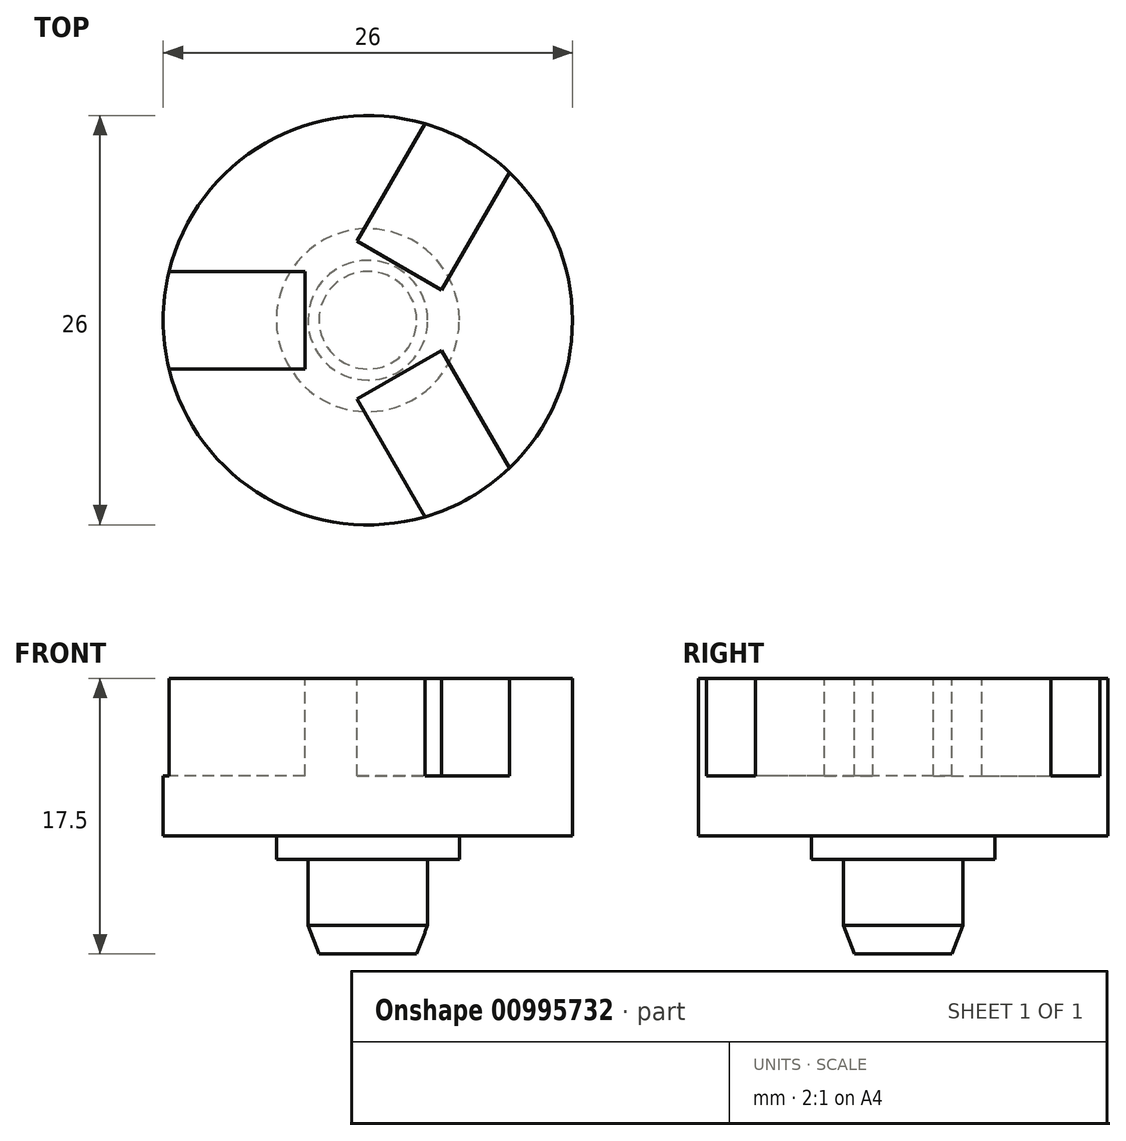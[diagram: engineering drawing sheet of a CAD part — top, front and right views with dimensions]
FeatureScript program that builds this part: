
annotation { "Feature Type Name" : "Feature", "Feature Type Description" : "" }
export const myFeature = defineFeature(function(context is Context, id is Id, definition is map)
    precondition{}
    {
        {
            var Q0;
            Q0=qCreatedBy(makeId("Front.planeOp"),FACE);
            var sketch = newSketch(context, id + "F0", { "sketchPlane" : qUnion([Q0])});
            skLineSegment(sketch, "E0", {"start": v(0, 0) * mm, "end": v(3.1, 0) * mm});
            skLineSegment(sketch, "E1", {"start": v(3.1, 0) * mm, "end": v(3.8, 1.83) * mm});
            skLineSegment(sketch, "E2", {"start": v(3.8, 1.83) * mm, "end": v(3.8, 6) * mm});
            skLineSegment(sketch, "E3", {"start": v(3.8, 6) * mm, "end": v(5.81, 6) * mm});
            skLineSegment(sketch, "E4", {"start": v(5.81, 6) * mm, "end": v(5.81, 7.5) * mm});
            skLineSegment(sketch, "E5", {"start": v(5.81, 7.5) * mm, "end": v(13, 7.5) * mm});
            skLineSegment(sketch, "E6", {"start": v(13, 7.5) * mm, "end": v(13, 17.5) * mm});
            skLineSegment(sketch, "E7", {"start": v(13, 17.5) * mm, "end": v(0, 17.5) * mm});
            skLineSegment(sketch, "E8", {"start": v(0, 17.5) * mm, "end": v(0, 0) * mm});
            skSolve(sketch);
        }
        {
            var Q0;
            Q0=makeQuery(id+"F0.imprint","IMPRINT",FACE,{"disambiguationData":[TD([[makeQuery(id+"F0.imprint","IMPRINT",EDGE,{"derivedFrom":sQuery(id+"F0.wireOp",EDGE,"E0")}),1.0]])]});
            var Q1;
            Q1=sQuery(id+"F0.wireOp",EDGE,"E8");
            revolve(context, id + "F1", {"surfaceOperationType" : NewSurfaceOperationType.NEW, "entities" : qUnion([Q0]), "axis" : qUnion([Q1]), "revolveType" : RevolveType.FULL});
        }
        {
            var Q0;
            Q0=makeQuery(id+"F1.opRevolve","SWEPT_FACE",FACE,{"disambiguationData":[OSD([sQuery(id+"F0.wireOp",EDGE,"E7")])]});
            var sketch = newSketch(context, id + "F2", { "sketchPlane" : qUnion([Q0])});
            skLineSegment(sketch, "E9.bottom", {"start": v(-4, 3.1) * mm, "end": v(-34.21, 3.1) * mm});
            skLineSegment(sketch, "E9.top", {"start": v(-4, -3.1) * mm, "end": v(-34.21, -3.1) * mm});
            skLineSegment(sketch, "E9.left", {"start": v(-4, 3.1) * mm, "end": v(-4, -3.1) * mm});
            skLineSegment(sketch, "E9.right", {"start": v(-34.21, 3.1) * mm, "end": v(-34.21, -3.1) * mm});
            skPoint(sketch, "E9.middle", {"position": v(-19.1, 0) * mm});
            skSolve(sketch);
        }
        {
            var Q0;
            {var subQ0=sQuery(id+"F2.wireOp",EDGE,"E9.left");Q0=makeQuery(id+"F2.imprint","IMPRINT",FACE,{"disambiguationData":[TD([[makeQuery(id+"F2.imprint","IMPRINT",EDGE,{"derivedFrom":subQ0}),-1.0]])]});}
            extrude(context, id + "F3", {"entities" : qUnion([Q0]), "oppositeDirection" : true, "depth" : 6.2 * mm, "offsetDistance" : 25 * mm});
        }
        {
            var Q0;
            Q0=makeQuery(id+"F3.opExtrude","SWEPT_BODY",BODY,{"disambiguationData":[OSD([sQuery(id+"F0.wireOp",EDGE,"E6"),sQuery(id+"F0.wireOp",EDGE,"E7"),sQuery(id+"F2.wireOp",EDGE,"E9.bottom"),sQuery(id+"F2.wireOp",EDGE,"E9.top"),sQuery(id+"F2.wireOp",EDGE,"E9.left")])]});
            var Q1;
            Q1=makeQuery(id+"F1.opRevolve","SWEPT_EDGE",EDGE,{"disambiguationData":[OSD([sQuery(id+"F0.wireOp",EDGE,"E6"),sQuery(id+"F0.wireOp",EDGE,"E7")])]});
            circularPattern(context, id + "F4", {"entities" : qUnion([Q0]), "axis" : qUnion([Q1]), "angle" : 360 * degree, "instanceCount" : 3, "equalSpace" : true});
        }
        {
            var Q0;
            Q0=makeQuery(id+"F3.opExtrude","SWEPT_BODY",BODY,{"disambiguationData":[OSD([sQuery(id+"F0.wireOp",EDGE,"E6"),sQuery(id+"F0.wireOp",EDGE,"E7"),sQuery(id+"F2.wireOp",EDGE,"E9.bottom"),sQuery(id+"F2.wireOp",EDGE,"E9.top"),sQuery(id+"F2.wireOp",EDGE,"E9.left")])]});
            var Q1;
            Q1=makeQuery(id+"F4.opPattern","COPY",BODY,{"derivedFrom":makeQuery(id+"F3.opExtrude","SWEPT_BODY",BODY,{"disambiguationData":[OSD([sQuery(id+"F0.wireOp",EDGE,"E6"),sQuery(id+"F0.wireOp",EDGE,"E7"),sQuery(id+"F2.wireOp",EDGE,"E9.bottom"),sQuery(id+"F2.wireOp",EDGE,"E9.top"),sQuery(id+"F2.wireOp",EDGE,"E9.left")])]}),"instanceName":"1"});
            var Q2;
            Q2=makeQuery(id+"F4.opPattern","COPY",BODY,{"derivedFrom":makeQuery(id+"F3.opExtrude","SWEPT_BODY",BODY,{"disambiguationData":[OSD([sQuery(id+"F0.wireOp",EDGE,"E6"),sQuery(id+"F0.wireOp",EDGE,"E7"),sQuery(id+"F2.wireOp",EDGE,"E9.bottom"),sQuery(id+"F2.wireOp",EDGE,"E9.top"),sQuery(id+"F2.wireOp",EDGE,"E9.left")])]}),"instanceName":"2"});
            var Q3;
            Q3=makeQuery(id+"F1.opRevolve","SWEPT_BODY",BODY,{"disambiguationData":[OSD([sQuery(id+"F0.wireOp",EDGE,"E0"),sQuery(id+"F0.wireOp",EDGE,"E1"),sQuery(id+"F0.wireOp",EDGE,"E2"),sQuery(id+"F0.wireOp",EDGE,"E3"),sQuery(id+"F0.wireOp",EDGE,"E4"),sQuery(id+"F0.wireOp",EDGE,"E5"),sQuery(id+"F0.wireOp",EDGE,"E6"),sQuery(id+"F0.wireOp",EDGE,"E7"),sQuery(id+"F0.wireOp",EDGE,"E8")])]});
            booleanBodies(context, id + "F5", {"operationType" : BooleanOperationType.SUBTRACTION, "tools" : qUnion([Q0, Q1, Q2]), "targets" : qUnion([Q3])});
        }
    });
